# Revit family: Proxway_Бесконтактная_кнопка_выхода_врезная_PW-704 B
name_source: partatom
category: Охранная сигнализация
units: mm (PartAtom-declared; Revit-internal decimal feet)

## family parameters
Всегда вертикально = Нет
На основе рабочей плоскости = Нет
Общий = Да
При загрузке вырезать с полостями = Нет
Размер круглого соединителя = Использовать диаметр
Сохранять ориентацию аннотаций = Нет
Тип детали = Нормальный
Точка расчета площади = Да

## types (2) — shared parameters
=Габариты= = =Габариты=
ADSK_Единица измерения = шт.
ADSK_Завод-изготовитель = ProxWay
ADSK_Количество = 1
ADSK_Марка = PW-704 B
ADSK_Наименование = Врезная бесконтактная кнопка выхода для СКУД
ADSK_Обозначение = SB
ADSK_Раздел спецификации = 3. Периферийное оборудование
ADSK_Размер_Высота = 86 мм
ADSK_Размер_Глубина = 15 мм
ADSK_Размер_Ширина = 86 мм
ADSK_Тип = PW-704 B
URL = https://proxway-ble.ru
Глубина_лицевая = 2 мм
Зона обслуживания_Отступ от прибора = 50 мм
Текст модели = PW-704 B
УГО_Тип = УГО_СС_Кнопка : УГО_Кнопка
zero-valued in all types: Отметка по умолчанию

## per-type parameters (varying)
| type | ADSK_Код изделия | Бокс для накладного монтажа |
| PW-704 B_Накладная бесконтактная кнопка выхода для СКУД без бокса |  | Нет |
| PW-704 B_Накладная бесконтактная кнопка выхода для СКУД с боксом | с боксом накладного монтажа | Да |
